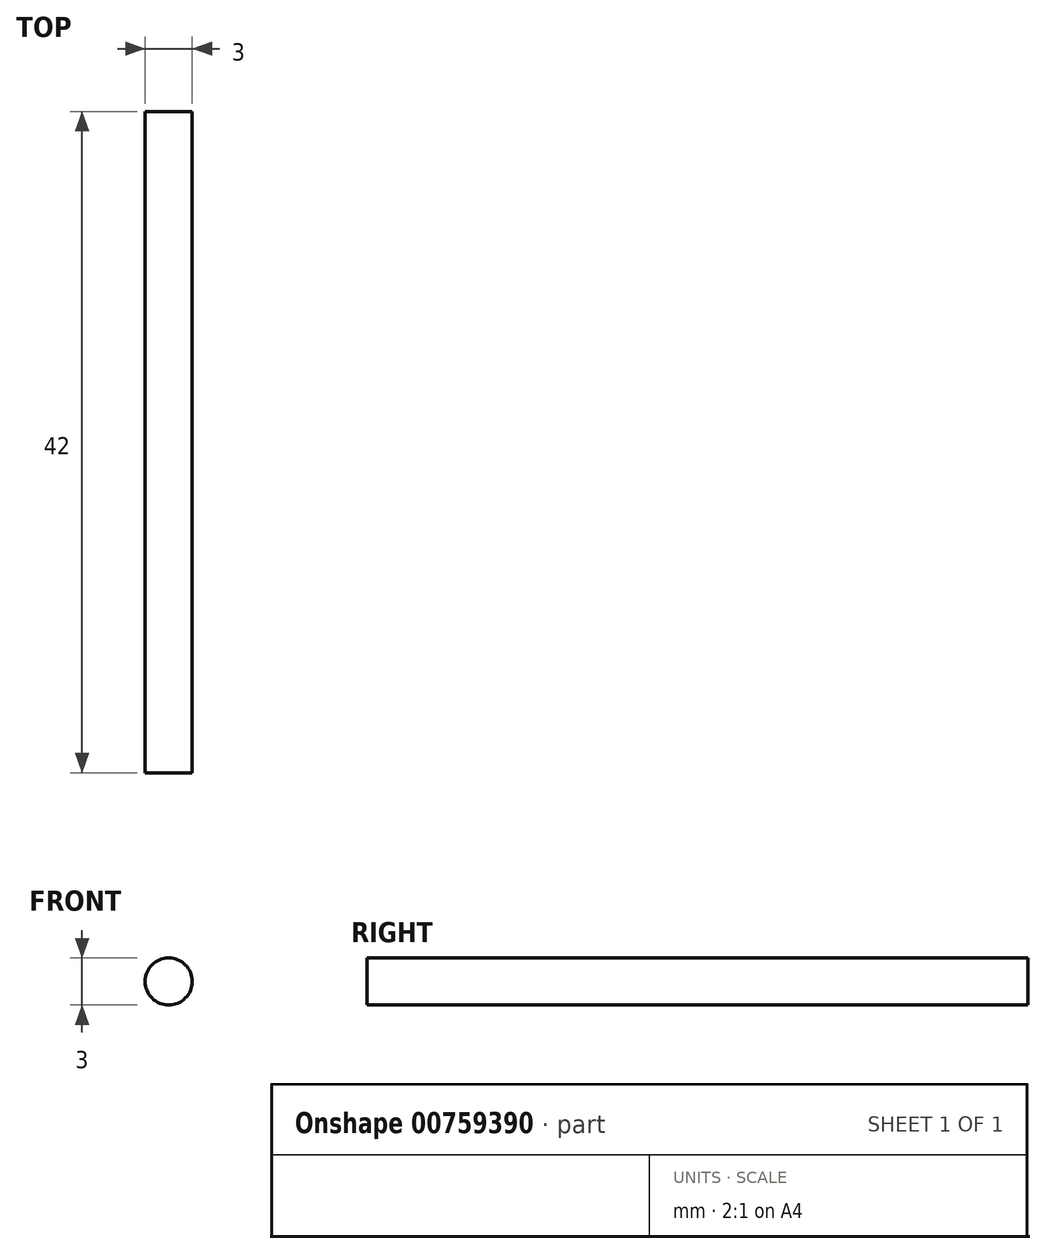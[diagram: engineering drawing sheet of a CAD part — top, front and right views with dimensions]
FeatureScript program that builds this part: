
annotation { "Feature Type Name" : "Feature", "Feature Type Description" : "" }
export const myFeature = defineFeature(function(context is Context, id is Id, definition is map)
    precondition{}
    {
        {
            var Q0;
            Q0=qCreatedBy(makeId("Front.planeOp"),FACE);
            var sketch = newSketch(context, id + "F0", { "sketchPlane" : qUnion([Q0])});
            skCircle(sketch, "E0", {"center": v(0, 0) * mm, "radius": 1.5 * mm});
            skSolve(sketch);
        }
        {
            var Q0;
            Q0=makeQuery(id+"F0.imprint","IMPRINT",FACE,{"disambiguationData":[TD([[makeQuery(id+"F0.imprint","IMPRINT",EDGE,{"derivedFrom":sQuery(id+"F0.wireOp",EDGE,"E0")}),1.0]])]});
            extrude(context, id + "F1", {"entities" : qUnion([Q0]), "oppositeDirection" : true, "depth" : 42 * mm, "offsetDistance" : 25 * mm});
        }
    });
